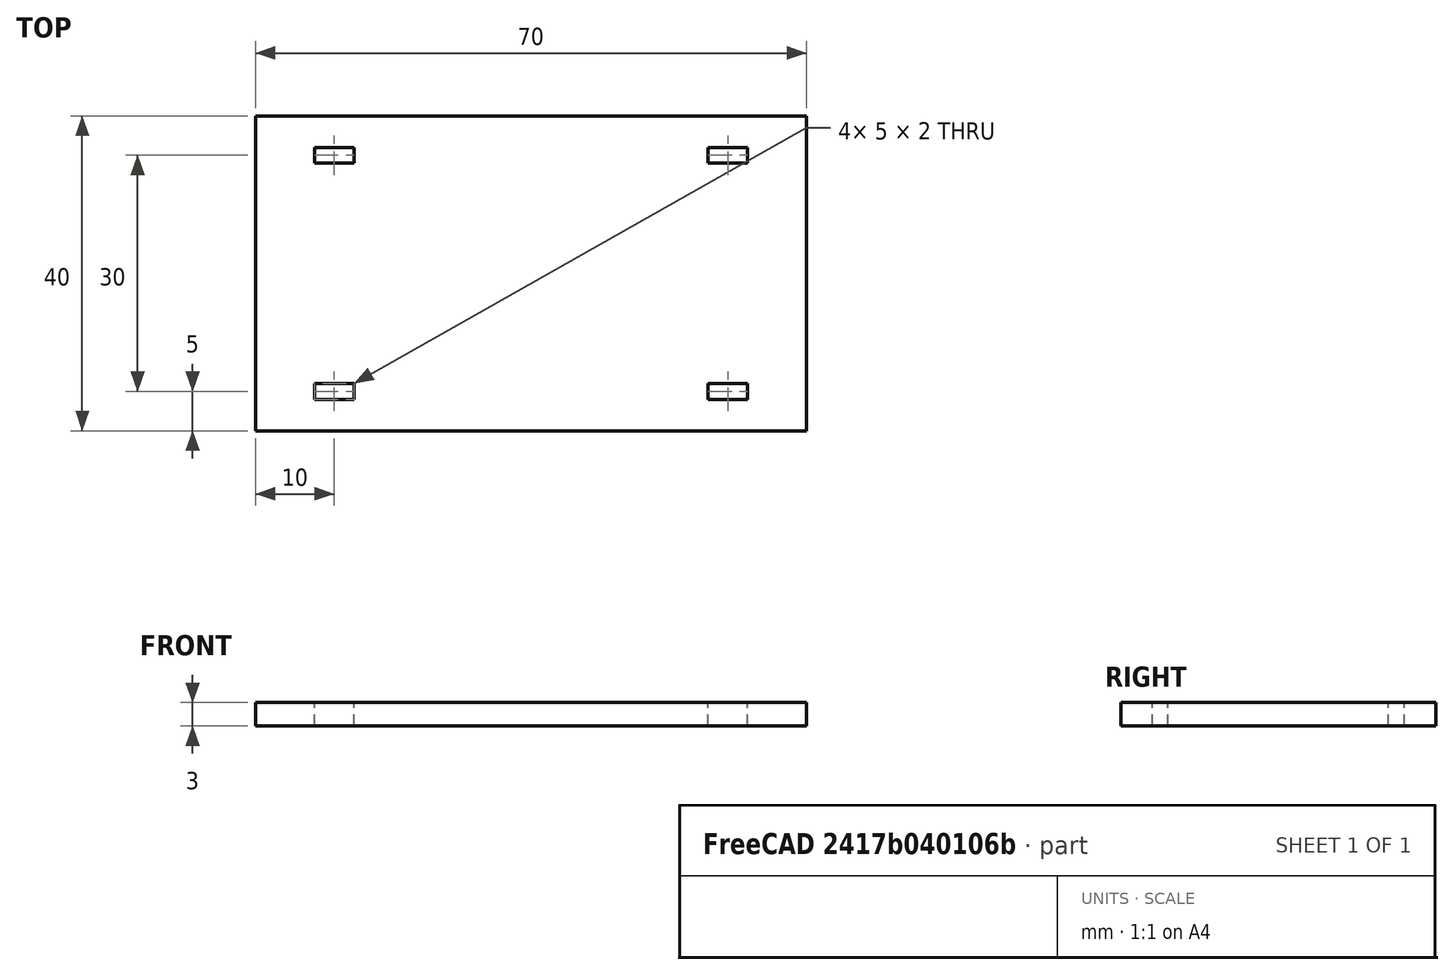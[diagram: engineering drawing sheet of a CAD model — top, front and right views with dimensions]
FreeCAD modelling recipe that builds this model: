
FCSTD DOCUMENT  (FreeCAD 0.17R13509 (Git))
Label: OuterBearingHolder
License: All rights reserved
LicenseURL: http://en.wikipedia.org/wiki/All_rights_reserved
objects: Sketcher::SketchObject×1, PartDesign::Pad×1, PartDesign::Body×1
note: 4 computed .brp shape members not serialized (recipe doc carries the construction recipe); baked Part::Feature solids carry a one-line shape summary decoded from their .brp

FEATURE [Sketcher::SketchObject] Sketch
  MapMode = 5
  Support = -> [XY_Plane]
  sketch-geometry (24):
    g0: LineSegment StartX=-35 StartY=20 StartZ=0 EndX=35 EndY=20 EndZ=0
    g1: LineSegment StartX=35 StartY=20 StartZ=0 EndX=35 EndY=-20 EndZ=0
    g2: LineSegment StartX=35 StartY=-20 StartZ=0 EndX=-35 EndY=-20 EndZ=0
    g3: LineSegment StartX=-35 StartY=-20 StartZ=0 EndX=-35 EndY=20 EndZ=0
    g4: LineSegment [constr] StartX=-25 StartY=20 StartZ=0 EndX=-25 EndY=-20 EndZ=0
    g5: LineSegment [constr] StartX=25 StartY=20 StartZ=0 EndX=25 EndY=-20 EndZ=0
    g6: LineSegment [constr] StartX=-35 StartY=-15 StartZ=0 EndX=35 EndY=-15 EndZ=0
    g7: LineSegment [constr] StartX=35 StartY=15 StartZ=0 EndX=-35 EndY=15 EndZ=0
    g8: LineSegment StartX=-27.5 StartY=16 StartZ=0 EndX=-22.5 EndY=16 EndZ=0
    g9: LineSegment StartX=-22.5 StartY=16 StartZ=0 EndX=-22.5 EndY=14 EndZ=0
    g10: LineSegment StartX=-22.5 StartY=14 StartZ=0 EndX=-27.5 EndY=14 EndZ=0
    g11: LineSegment StartX=-27.5 StartY=14 StartZ=0 EndX=-27.5 EndY=16 EndZ=0
    g12: LineSegment StartX=22.5 StartY=16 StartZ=0 EndX=27.5 EndY=16 EndZ=0
    g13: LineSegment StartX=27.5 StartY=16 StartZ=0 EndX=27.5 EndY=14 EndZ=0
    g14: LineSegment StartX=27.5 StartY=14 StartZ=0 EndX=22.5 EndY=14 EndZ=0
    g15: LineSegment StartX=22.5 StartY=14 StartZ=0 EndX=22.5 EndY=16 EndZ=0
    g16: LineSegment StartX=22.5 StartY=-14 StartZ=0 EndX=27.5 EndY=-14 EndZ=0
    g17: LineSegment StartX=27.5 StartY=-14 StartZ=0 EndX=27.5 EndY=-16 EndZ=0
    g18: LineSegment StartX=27.5 StartY=-16 StartZ=0 EndX=22.5 EndY=-16 EndZ=0
    g19: LineSegment StartX=22.5 StartY=-16 StartZ=0 EndX=22.5 EndY=-14 EndZ=0
    g20: LineSegment StartX=-27.5 StartY=-14 StartZ=0 EndX=-22.5 EndY=-14 EndZ=0
    g21: LineSegment StartX=-22.5 StartY=-14 StartZ=0 EndX=-22.5 EndY=-16 EndZ=0
    g22: LineSegment StartX=-22.5 StartY=-16 StartZ=0 EndX=-27.5 EndY=-16 EndZ=0
    g23: LineSegment StartX=-27.5 StartY=-16 StartZ=0 EndX=-27.5 EndY=-14 EndZ=0
  constraints (70):
    c: Coincident(g0,g1)
    c: Coincident(g1,g2)
    c: Coincident(g2,g3)
    c: Coincident(g3,g0)
    c: Horizontal(g2)
    c: Vertical(g1)
    c: Symmetric(g0,g0,g-2)
    c: Symmetric(g2,g0,g-1)
    c: DistanceX(g0,g0) = 70
    c: DistanceY(g3,g3) = 40
    c: PointOnObject(g4,g0)
    c: PointOnObject(g4,g2)
    c: PointOnObject(g5,g0)
    c: PointOnObject(g5,g2)
    c: PointOnObject(g6,g3)
    c: PointOnObject(g6,g1)
    c: PointOnObject(g7,g3)
    c: Symmetric(g4,g5,g-2)
    c: Symmetric(g7,g6,g-1)
    c: PointOnObject(g7,g1)
    c: DistanceY(g6,g7) = 30
    c: DistanceX(g4,g5) = 50
    c: Coincident(g8,g9)
    c: Coincident(g9,g10)
    c: Coincident(g10,g11)
    c: Coincident(g11,g8)
    c: Horizontal(g8)
    c: Horizontal(g10)
    c: Vertical(g9)
    c: Vertical(g11)
    c: Coincident(g12,g13)
    c: Coincident(g13,g14)
    c: Coincident(g14,g15)
    c: Coincident(g15,g12)
    c: Horizontal(g12)
    c: Horizontal(g14)
    c: Vertical(g13)
    c: Vertical(g15)
    c: Coincident(g16,g17)
    c: Coincident(g17,g18)
    c: Coincident(g18,g19)
    c: Coincident(g19,g16)
    c: Horizontal(g16)
    c: Horizontal(g18)
    c: Vertical(g17)
    c: Vertical(g19)
    c: Coincident(g20,g21)
    c: Coincident(g21,g22)
    c: Coincident(g22,g23)
    c: Coincident(g23,g20)
    c: Horizontal(g20)
    c: Horizontal(g22)
    c: Vertical(g21)
    c: Vertical(g23)
    c: Symmetric(g20,g20,g4)
    c: Symmetric(g20,g22,g6)
    c: Symmetric(g8,g8,g4)
    c: Symmetric(g10,g8,g7)
    c: Symmetric(g12,g12,g5)
    c: Symmetric(g12,g14,g7)
    c: Symmetric(g16,g16,g5)
    c: Symmetric(g18,g16,g6)
    c: DistanceX(g8,g8) = 5
    c: DistanceY(g10,g8) = 2
    c: Equal(g8,g12)
    c: Equal(g12,g16)
    c: Equal(g16,g20)
    c: Equal(g11,g23)
    c: Equal(g23,g19)
    c: Equal(g19,g15)
FEATURE [PartDesign::Pad] Pad
  Length = 3
  Length2 = 100
  Profile = -> Sketch
  Refine = true
  Type = 0
FEATURE [PartDesign::Body] Body
  Group = -> [Sketch,Pad]
  Origin = -> Origin
  Tip = -> Pad
